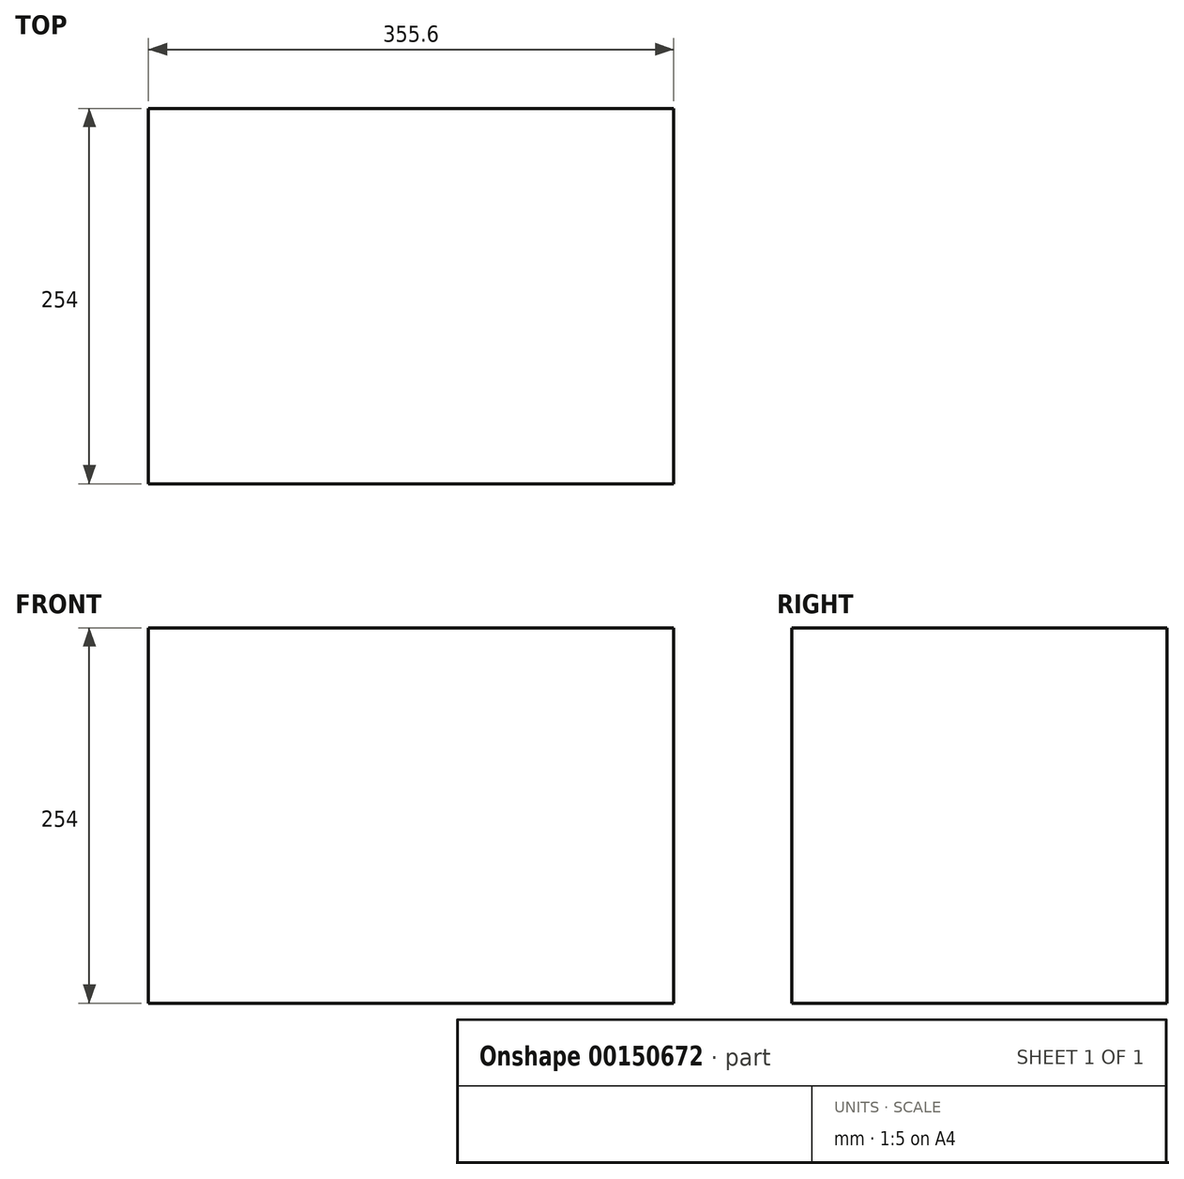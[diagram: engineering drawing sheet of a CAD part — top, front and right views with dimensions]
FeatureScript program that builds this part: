
annotation { "Feature Type Name" : "Feature", "Feature Type Description" : "" }
export const myFeature = defineFeature(function(context is Context, id is Id, definition is map)
    precondition{}
    {
        {
            var Q0;
            Q0=qCreatedBy(makeId("Top.planeOp"),FACE);
            var sketch = newSketch(context, id + "F0", { "sketchPlane" : qUnion([Q0])});
            skLineSegment(sketch, "E0.bottom", {"start": v(-175.76, 157.61) * mm, "end": v(179.84, 157.61) * mm});
            skLineSegment(sketch, "E0.top", {"start": v(-175.76, -96.39) * mm, "end": v(179.84, -96.39) * mm});
            skLineSegment(sketch, "E0.left", {"start": v(-175.76, 157.61) * mm, "end": v(-175.76, -96.39) * mm});
            skLineSegment(sketch, "E0.right", {"start": v(179.84, 157.61) * mm, "end": v(179.84, -96.39) * mm});
            skSolve(sketch);
        }
        {
            var Q0;
            Q0 = qSketchRegion(id + "F0", true);
            extrude(context, id + "F1", {"entities" : qUnion([Q0]), "depth" : 254 * mm});
        }
    });
